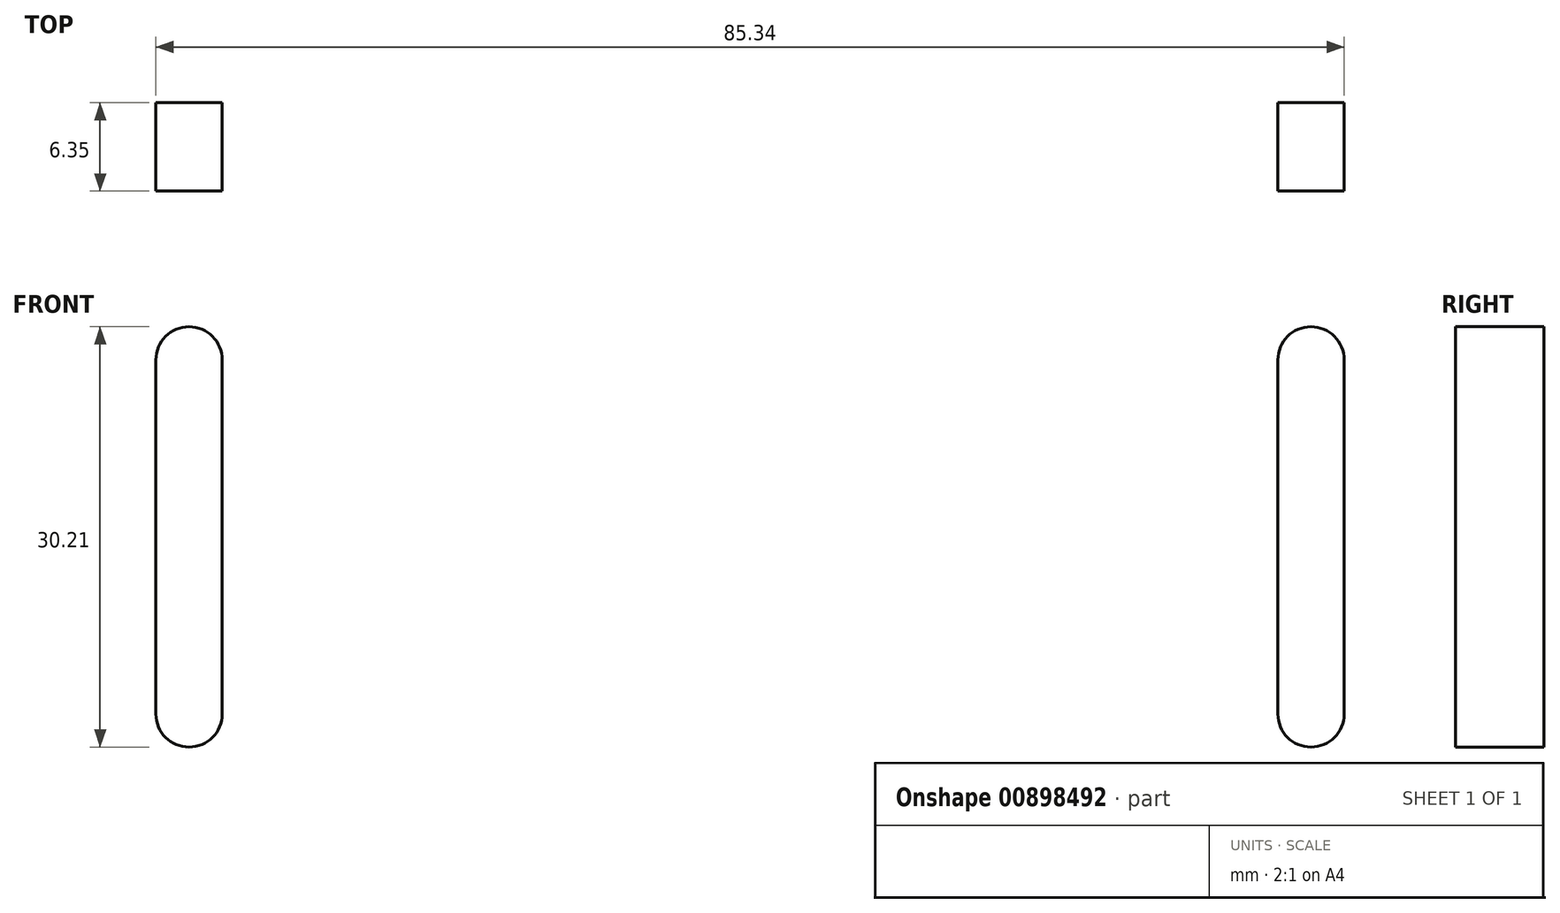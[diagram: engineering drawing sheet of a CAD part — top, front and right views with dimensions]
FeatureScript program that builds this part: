
annotation { "Feature Type Name" : "Feature", "Feature Type Description" : "" }
export const myFeature = defineFeature(function(context is Context, id is Id, definition is map)
    precondition{}
    {
        {
            var Q0;
            Q0=qCreatedBy(makeId("Front.planeOp"),FACE);
            var sketch = newSketch(context, id + "F0", { "sketchPlane" : qUnion([Q0])});
            skLineSegment(sketch, "E0.bottom", {"start": v(52, -25.4) * mm, "end": v(-52, -25.4) * mm});
            skLineSegment(sketch, "E0.top", {"start": v(52, 25.4) * mm, "end": v(-52, 25.4) * mm});
            skLineSegment(sketch, "E0.left", {"start": v(52, -25.4) * mm, "end": v(52, 25.4) * mm});
            skLineSegment(sketch, "E0.right", {"start": v(-52, -25.4) * mm, "end": v(-52, 25.4) * mm});
            skPoint(sketch, "E0.middle", {"position": v(0, 0) * mm});
            skSolve(sketch);
        }
        {
            var Q0;
            Q0=makeQuery(id+"F0.imprint","IMPRINT",FACE,{"disambiguationData":[TD([[makeQuery(id+"F0.imprint","IMPRINT",EDGE,{"derivedFrom":sQuery(id+"F0.wireOp",EDGE,"E0.bottom")}),-1.0]])]});
            extrude(context, id + "F1", {"entities" : qUnion([Q0]), "depth" : 6.35 * mm, "offsetDistance" : 25.4 * mm});
        }
        {
            var Q0;
            Q0=makeQuery(id+"F1.opExtrude","SWEPT_FACE",FACE,{"disambiguationData":[OSD([sQuery(id+"F0.wireOp",EDGE,"E0.top")])]});
            var sketch = newSketch(context, id + "F2", { "sketchPlane" : qUnion([Q0])});
            skLineSegment(sketch, "E1.bottom", {"start": v(-52, 0) * mm, "end": v(52, 0) * mm});
            skLineSegment(sketch, "E1.top", {"start": v(-52, -50.8) * mm, "end": v(52, -50.8) * mm});
            skLineSegment(sketch, "E1.left", {"start": v(-52, 0) * mm, "end": v(-52, -50.8) * mm});
            skLineSegment(sketch, "E1.right", {"start": v(52, 0) * mm, "end": v(52, -50.8) * mm});
            skSolve(sketch);
        }
        {
            var Q0;
            {var subQ0=sQuery(id+"F2.wireOp",EDGE,"E1.top");Q0=makeQuery(id+"F2.imprint","IMPRINT",FACE,{"disambiguationData":[TD([[makeQuery(id+"F2.imprint","IMPRINT",EDGE,{"derivedFrom":subQ0}),1.0]])]});}
            extrude(context, id + "F3", {"entities" : qUnion([Q0]), "operationType" : NewBodyOperationType.ADD, "oppositeDirection" : true, "depth" : 6.35 * mm, "offsetDistance" : 25.4 * mm});
        }
        {
            var Q0;
            Q0=makeQuery(id+"F1.opExtrude","CAP_FACE",FACE,{"disambiguationData":[OSD([sQuery(id+"F0.wireOp",EDGE,"E0.bottom"),sQuery(id+"F0.wireOp",EDGE,"E0.top"),sQuery(id+"F0.wireOp",EDGE,"E0.left"),sQuery(id+"F0.wireOp",EDGE,"E0.right")])],"isStart":true});
            var sketch = newSketch(context, id + "F4", { "sketchPlane" : qUnion([Q0])});
            skLineSegment(sketch, "E2", {"start": v(40.29, -18.4) * mm, "end": v(40.29, 7.05) * mm});
            skLineSegment(sketch, "E3.MirrorCS", {"start": v(-40.29, -18.4) * mm, "end": v(-40.29, 7.05) * mm});
            skArc(sketch, "E4.0.startCap", {"start": v(42.67, -18.4) * mm, "mid": v(40.29, -20.78) * mm, "end": v(37.9, -18.4) * mm});
            skArc(sketch, "E4.0.endCap", {"start": v(37.9, 7.05) * mm, "mid": v(40.29, 9.43) * mm, "end": v(42.67, 7.05) * mm});
            skLineSegment(sketch, "E4.0.left", {"start": v(37.9, -18.4) * mm, "end": v(37.9, 7.05) * mm});
            skLineSegment(sketch, "E4.0.right", {"start": v(42.67, -18.4) * mm, "end": v(42.67, 7.05) * mm});
            skArc(sketch, "E4.1.startCap", {"start": v(-37.9, -18.4) * mm, "mid": v(-40.29, -20.78) * mm, "end": v(-42.67, -18.4) * mm});
            skArc(sketch, "E4.1.endCap", {"start": v(-42.67, 7.05) * mm, "mid": v(-40.29, 9.43) * mm, "end": v(-37.9, 7.05) * mm});
            skLineSegment(sketch, "E4.1.left", {"start": v(-42.67, -18.4) * mm, "end": v(-42.67, 7.05) * mm});
            skLineSegment(sketch, "E4.1.right", {"start": v(-37.9, -18.4) * mm, "end": v(-37.9, 7.05) * mm});
            skSolve(sketch);
        }
        {
            var Q0;
            {var subQ0=sQuery(id+"F0.wireOp",EDGE,"E0.top");Q0=makeQuery(id+"F3.boolean.opBoolean","MERGE",FACE,{"derivedFrom":[makeQuery(id+"F1.opExtrude","SWEPT_FACE",FACE,{"disambiguationData":[OSD([subQ0])]}),makeQuery(id+"F3.opExtrude","CAP_FACE",FACE,{"disambiguationData":[OSD([subQ0,sQuery(id+"F2.wireOp",EDGE,"E1.top"),sQuery(id+"F2.wireOp",EDGE,"E1.left"),sQuery(id+"F2.wireOp",EDGE,"E1.right")])],"isStart":true})]});}
            var sketch = newSketch(context, id + "F5", { "sketchPlane" : qUnion([Q0])});
            skPoint(sketch, "E5", {"position": v(0, -28.58) * mm});
            skSolve(sketch);
        }
        {
            var Q0;
            Q0=sQuery(id+"F5.wireOp",VERTEX,"E5");
            var Q1;
            Q1=makeQuery(id+"F1.opExtrude","SWEPT_BODY",BODY,{"disambiguationData":[OSD([sQuery(id+"F0.wireOp",EDGE,"E0.bottom"),sQuery(id+"F0.wireOp",EDGE,"E0.top"),sQuery(id+"F0.wireOp",EDGE,"E0.left"),sQuery(id+"F0.wireOp",EDGE,"E0.right")])]});
            hole(context, id + "F6", {"style" : HoleStyle.SIMPLE, "endStyle" : HoleEndStyle.THROUGH, "holeDiameter" : 23 / 812.8 * mm, "majorDiameter" : 5 * mm, "isTappedThrough" : true, "tappedDepth" : 7.9 * mm, "tapClearance" : 3, "startFromSketch" : true, "locations" : qUnion([Q0]), "scope" : qUnion([Q1])});
        }
        {
            var Q0;
            {var subQ0=sQuery(id+"F0.wireOp",EDGE,"E0.top");Q0=makeQuery(id+"F3.boolean.opBoolean","MERGE",FACE,{"derivedFrom":[makeQuery(id+"F1.opExtrude","SWEPT_FACE",FACE,{"disambiguationData":[OSD([subQ0])]}),makeQuery(id+"F3.opExtrude","CAP_FACE",FACE,{"disambiguationData":[OSD([subQ0,sQuery(id+"F2.wireOp",EDGE,"E1.top"),sQuery(id+"F2.wireOp",EDGE,"E1.left"),sQuery(id+"F2.wireOp",EDGE,"E1.right")])],"isStart":true})]});}
            var sketch = newSketch(context, id + "F7", { "sketchPlane" : qUnion([Q0])});
            skLineSegment(sketch, "E6", {"start": v(-52, -19.05) * mm, "end": v(-29.78, -19.05) * mm});
            skLineSegment(sketch, "E7", {"start": v(-20.25, -28.58) * mm, "end": v(-20.25, -50.8) * mm});
            skLineSegment(sketch, "E8", {"start": v(-20.25, -50.8) * mm, "end": v(-52, -50.8) * mm});
            skLineSegment(sketch, "E9", {"start": v(-52, -50.8) * mm, "end": v(-52, -19.05) * mm});
            skPoint(sketch, "E10.visualSharp", {"position": v(-20.25, -19.05) * mm});
            skArc(sketch, "E10.filletArc", {"start": v(-20.25, -28.58) * mm, "mid": v(-23.04, -21.84) * mm, "end": v(-29.78, -19.05) * mm});
            skLineSegment(sketch, "E11.MirrorCS", {"start": v(52, -19.05) * mm, "end": v(29.78, -19.05) * mm});
            skArc(sketch, "E12.MirrorCS", {"start": v(20.25, -28.58) * mm, "mid": v(23.04, -21.84) * mm, "end": v(29.78, -19.05) * mm});
            skLineSegment(sketch, "E13.MirrorCS", {"start": v(20.25, -28.58) * mm, "end": v(20.25, -50.8) * mm});
            skLineSegment(sketch, "E14.MirrorCS", {"start": v(20.25, -50.8) * mm, "end": v(52, -50.8) * mm});
            skLineSegment(sketch, "E15.MirrorCS", {"start": v(52, -50.8) * mm, "end": v(52, -19.05) * mm});
            skSolve(sketch);
        }
        {
            var Q0;
            Q0=makeQuery(id+"F7.imprint","IMPRINT",FACE,{"disambiguationData":[TD([[makeQuery(id+"F7.imprint","IMPRINT",EDGE,{"derivedFrom":sQuery(id+"F7.wireOp",EDGE,"E6")}),-1.0]])]});
            var Q1;
            Q1=makeQuery(id+"F7.imprint","IMPRINT",FACE,{"disambiguationData":[TD([[makeQuery(id+"F7.imprint","IMPRINT",EDGE,{"derivedFrom":sQuery(id+"F7.wireOp",EDGE,"E11.MirrorCS")}),1.0]])]});
            extrude(context, id + "F8", {"entities" : qUnion([Q0, Q1]), "operationType" : NewBodyOperationType.REMOVE, "endBound" : BoundingType.THROUGH_ALL, "oppositeDirection" : true, "depth" : 25 * mm, "offsetDistance" : 25 * mm});
        }
        {
            var Q0;
            Q0=makeQuery(id+"F4.imprint","IMPRINT",FACE,{"disambiguationData":[TD([[makeQuery(id+"F4.imprint","IMPRINT",EDGE,{"derivedFrom":sQuery(id+"F4.wireOp",EDGE,"E4.0.startCap")}),-1.0]])]});
            var Q1;
            Q1=makeQuery(id+"F4.imprint","IMPRINT",FACE,{"disambiguationData":[TD([[makeQuery(id+"F4.imprint","IMPRINT",EDGE,{"derivedFrom":sQuery(id+"F4.wireOp",EDGE,"E4.1.startCap")}),-1.0]])]});
            extrude(context, id + "F9", {"entities" : qUnion([Q0, Q1]), "operationType" : NewBodyOperationType.REMOVE, "endBound" : BoundingType.THROUGH_ALL, "oppositeDirection" : true, "depth" : 25 * mm, "offsetDistance" : 25 * mm});
        }
    });
